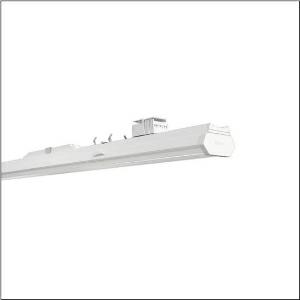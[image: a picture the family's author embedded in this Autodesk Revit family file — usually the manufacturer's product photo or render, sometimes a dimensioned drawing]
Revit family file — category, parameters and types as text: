
# Revit family: licross_11_protected_mo_51td1bdn68xg3s
name_source: partatom
category: Lighting Fixtures
units: mm (PartAtom-declared; Revit-internal decimal feet)

## family parameters
Cut with Voids When Loaded = No
Host = Face
Light Source = No
Part Type = Normal
Room Calculation Point = No
Round Connector Dimension = Use Diameter
Shared = No

## types (1)
- --- (1 x LED, 900 lm, 6.8 W, 6500K)
    Apparent Load = 7 VA
    CIE Flux Codes = 54 82 95 97 100
    Color Rendering = 80
    Color Temperature = 6500K
    Default Elevation = 1800 mm
    Description = Licross 11 Protected MO, luminaire insert, of sheet steel, galvanised, coil coated, white, length: 1.500mm, width: 90mm, height: 101mm, LED rated luminous flux: 8.310lm, light colour: 865, SDCM (Standard Deviation of Colour Matching)MacAdam ≤ 2 SDCM (initial), control gear: DALI 2 (for two DALI lines), with plug, 6-pole, with phase selection, for trunking rail, 14-core, mains connection: 220..240V, AC, 50/60Hz, rated input power: 55W, for trunking rail, 14-core, internal wiring halogen-free, for emergency light function, converter,control gear: single battery element, battery: LiFePO4, 9Ah, primary optical cover: cover, of PMMA, light emission: direct distribution, primary light characteristic: symmetric, protection rating (complete): IP54, insulation class (complete): insulation class I (protective earthing), certification: CE, UKCA, protection symbol: D if used in an environment with non-conductive dust loads with corresponding accessories, impact resistance: IK06, permissible ambient temperature for indoor applications: +5..+35°C, standard: EN 60598-2-22, corresponds to IFS (International Featured Standards) requirements for safety and quality in the food industry, reducing of maximum allowable ambient temperature of 5°C with ceiling mounting, LABS conformity tested according to VDMA 24364:2018-05, The light source and the operating device comply with the requirements of the Ecodesign Regulation (EU) 2019/2020 and are replaceable in accordance with this regulation, packaging unit: 1 piece
    Height = 92 mm
    Lamp = 1 x LED
    Lamp Light Flux = 900 lm
    Lamp Power = 6.8 W
    Lamp count = 1
    Length = 1500 mm
    Luminous efficacy = 132 lm/W
    Manufacturer = Siteco
    ModVariant = No
    Model = 51TD1BDN68XG3S
    Mounting Place = Ceiling
    Mounting Type = Pendant
    Number of Poles = 1
    OnlyDefault = Yes
    Power Factor = 1
    Product Name = Licross 11 Protected MO
    Product group = luminaire insert | ceiling pendant
    ProductGroupID = 901
    Protection Class = Protection class I
    Protection Degree = IP 54
    RLX_Detail_Level = 1
    RLX_Emergency_Light_Flux = 0 lm
    RLX_Emergency_Type = 0
    RLX_Emergency_Type_DB = No
    RlxData = <blob elided: 25089 chars, md5=75607555>
    Socket = socket
    Standby Power = 0 W
    System Light Flux = 900 lm
    System Power = 7 W
    Type Comments = : emergency light operation: 3 h
    Type Image = l_1256145.jpg
    URL = http://relux.com
    VarID = @adj_038111
    Voltage = 0 V
    Weight = 0.00 kg
    Width = 88 mm

## geometry (parser evidence)
native form markers: Blend x4, Sweep x13
no freeform markers — native parametric forms only
